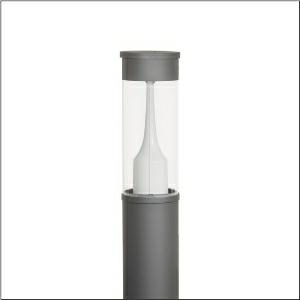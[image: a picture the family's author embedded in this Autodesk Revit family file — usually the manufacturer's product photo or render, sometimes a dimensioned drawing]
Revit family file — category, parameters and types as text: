
# Revit family: city-light_260_iq___st1_2a_5xa5295kf14h_47e0
name_source: partatom
category: Lighting Fixtures
units: mm (PartAtom-declared; Revit-internal decimal feet)

## family parameters
Cut with Voids When Loaded = No
Host = Face
Light Source = No
Part Type = Normal
Room Calculation Point = No
Round Connector Dimension = Use Diameter
Shared = No

## types (1)
- --- (1 x LED, 1540 lm, 10 W, 4000K)
    Apparent Load = 10 VA
    CIE Flux Codes = 22 61 93 96 100
    Color Rendering = 70
    Color Temperature = 4000K
    Default Elevation = 1800 mm
    Description = City-Light 260 iQ, light pillar, Module 540 iQ-SR, primary light control with 3 zone facetted reflector, of plastic, silver coated, highly specular, structured, primary optical cover: cover, of PMMA, transparent, partly coated, light distribution: ST1.2a, primary light characteristic: asymmetric, LED, High Power LED, rated luminous flux: 1.540lm, luminous efficacy: 154lm/W, light colour: 740, colour temperature: 4000K, control gear: iQ Street-Remote, control: pre-setting: logarithmic dimming characteristic, Street-Remote, Auto-Match, Temp-Guard, Lumen-Switch, Night-Set, Smart-Wire, Light-Fading, Desk-Remote (wireless, voltage-free reading and setting of iQ features in the workshop via application-optimized NFC function/RFID function), optimised constant luminous flux control (CLO 2.0), with terminal, 6-pole, max. 2.5mm², mains connection: 230..240V, AC, 50/60Hz, start of lifetime: 10W, end of service life: 10W, reduction: 5W, luminaire housing, cylindrical, of extruded aluminium section, coated, Siteco® metallic grey (DB 702S), length: 2.600mm, diameter: 200mm, Module 540 iQ-SR, traffic white (RAL 9016), equipment: standard, protection rating (complete): IP65, insulation class (complete): insulation class II (safety insulation), certification: CE, ENEC, VDE, packaging unit: 1 piece

Light Distribution: ST1.2a
    Height = 500 mm
    Lamp = 1 x LED
    Lamp Light Flux = 1540 lm
    Lamp Power = 10 W
    Lamp count = 1
    Length = 200 mm  [stored 0.656168 ft]
    Luminous efficacy = 154 lm/W
    Manufacturer = Siteco
    ModVariant = No
    Model = 5XA5295KF14H
    Mounting Place = Floor
    Mounting Type = Freestanding
    Number of Poles = 1
    OnlyDefault = Yes
    Power Factor = 1
    Product Name = City-Light 260 iQ | ST1.2a
    Product group = light pillar
    ProductGroupID = 1301
    Protection Class = Protection class II
    Protection Degree = IP 65
    RLX_Detail_Level = 1
    RLX_Emergency_Light_Flux = 0 lm
    RLX_Emergency_Type = 0
    RLX_Emergency_Type_DB = No
    RlxData = <blob elided: 64761 chars, md5=ff5397eb>
    Socket = socket
    Standby Power = 0 W
    System Light Flux = 1540 lm
    System Power = 10 W
    Type Comments = factory setting: luminous flux: 100 % | dim-lin: 254 | 401 mA
    Type Image = l_1006918.jpg
    URL = http://relux.com
    VarID = @adj_180637
    Voltage = 0 V
    Weight = 0.00 kg
    Width = 0 mm  [stored 0 ft]

note: [stored X ft] marks values corroborated as IEEE doubles in the binary element streams (Revit-internal decimal feet)

## geometry (parser evidence)
native form markers: Blend x4, Sweep x11
no freeform markers — native parametric forms only
